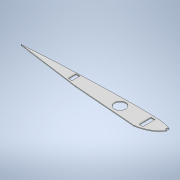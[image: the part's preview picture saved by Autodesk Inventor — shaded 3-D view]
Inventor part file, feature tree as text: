
AUTODESK INVENTOR PART (.ipt)
format: ipt  version: 2021 (Build 250183000, 183)  size: 143,872 bytes
history: native  units: mm
features: extrude x1, sketch x1
ambient origin geometry x8: Origin, YZ Plane, XZ Plane, XY Plane, X Axis, Y Axis, Z Axis, Center Point
bodies: Body1 (feature_tree)
feature tree (2):
  extrude  "Extrusion2"  Depth=2.0mm
  sketch  "Sketch1"  dims[d5=160.0mm d8=160.0mm d9=28.5mm d10=18.5mm d11=10.0mm d12=30.0mm d13=10.0mm d14=20.0mm d17=5.0mm d18=5.0mm d19=2.0mm d20=0.0mm]
